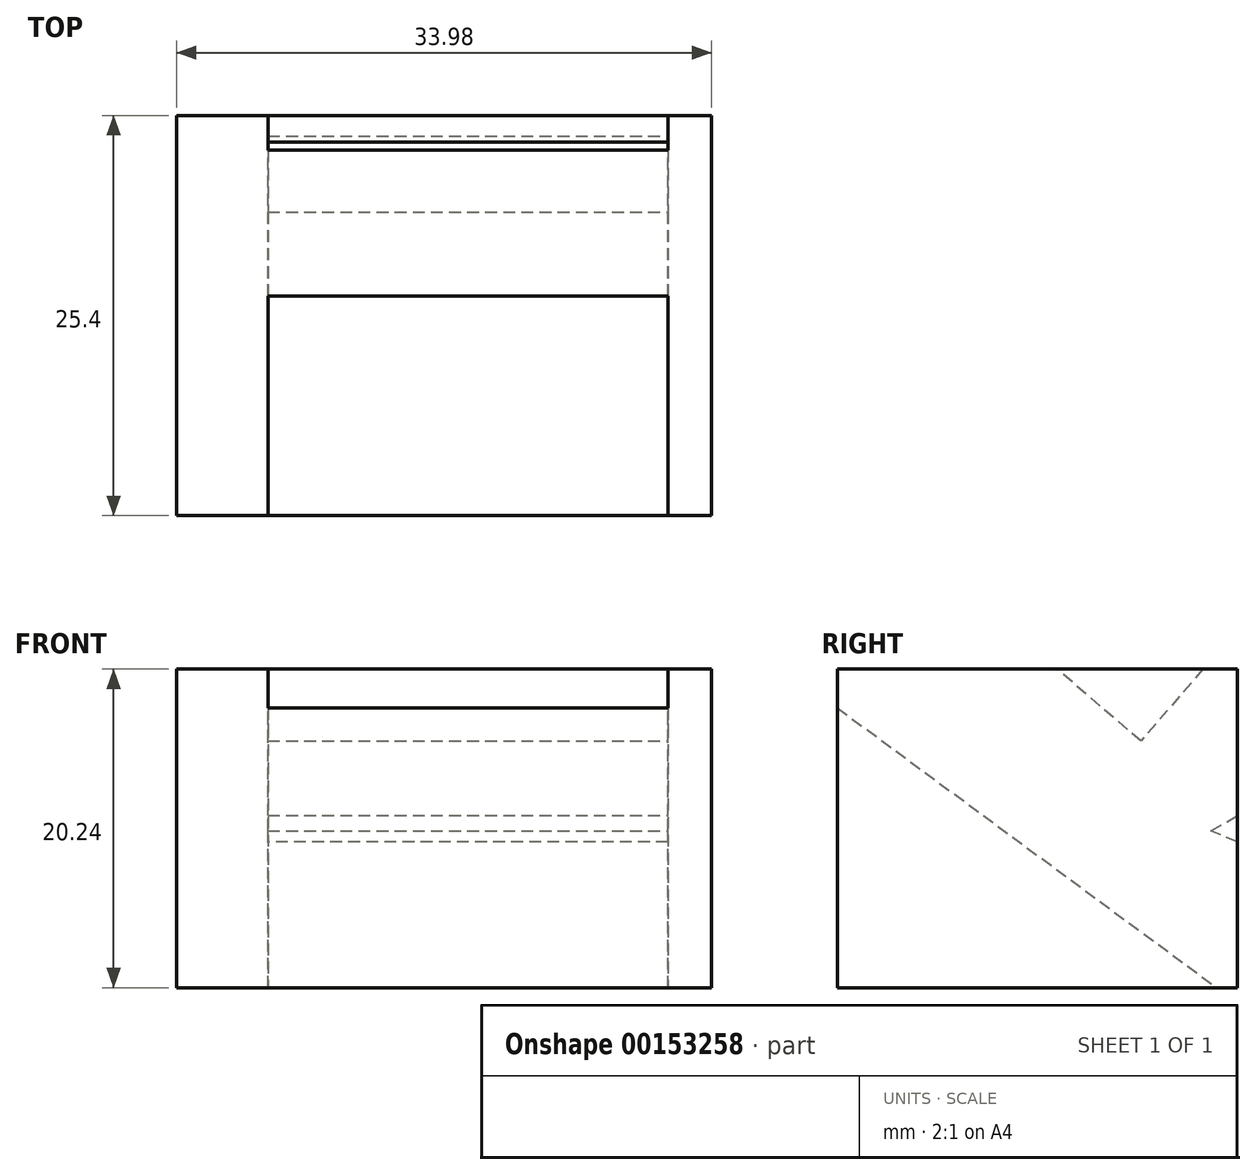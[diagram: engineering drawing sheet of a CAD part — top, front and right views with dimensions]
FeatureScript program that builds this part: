
annotation { "Feature Type Name" : "Feature", "Feature Type Description" : "" }
export const myFeature = defineFeature(function(context is Context, id is Id, definition is map)
    precondition{}
    {
        {
            var Q0;
            Q0=qCreatedBy(makeId("Front.planeOp"),FACE);
            var sketch = newSketch(context, id + "F0", { "sketchPlane" : qUnion([Q0])});
            skLineSegment(sketch, "E0.bottom", {"start": v(-18.5, 22.23) * mm, "end": v(15.48, 22.23) * mm});
            skLineSegment(sketch, "E0.top", {"start": v(-18.5, 1.99) * mm, "end": v(15.48, 1.99) * mm});
            skLineSegment(sketch, "E0.left", {"start": v(-18.5, 22.23) * mm, "end": v(-18.5, 1.99) * mm});
            skLineSegment(sketch, "E0.right", {"start": v(15.48, 22.23) * mm, "end": v(15.48, 1.99) * mm});
            skSolve(sketch);
        }
        {
            var Q0;
            Q0 = qSketchRegion(id + "F0", true);
            extrude(context, id + "F1", {"entities" : qUnion([Q0]), "depth" : 25.4 * mm});
        }
        {
            var Q0;
            Q0=qCreatedBy(makeId("Right.planeOp"),FACE);
            var sketch = newSketch(context, id + "F2", { "sketchPlane" : qUnion([Q0])});
            skLineSegment(sketch, "E1", {"start": v(-39.44, 30.1) * mm, "end": v(11.02, -7.1) * mm});
            skLineSegment(sketch, "E2", {"start": v(11.02, -7.1) * mm, "end": v(15.88, 4.72) * mm});
            skLineSegment(sketch, "E3", {"start": v(15.88, 4.72) * mm, "end": v(-1.68, 11.94) * mm});
            skLineSegment(sketch, "E4", {"start": v(-1.68, 11.94) * mm, "end": v(7.32, 17.2) * mm});
            skLineSegment(sketch, "E5", {"start": v(7.32, 17.2) * mm, "end": v(0, 26.2) * mm});
            skLineSegment(sketch, "E6", {"start": v(1.21, 26.2) * mm, "end": v(-6.14, 17.65) * mm});
            skLineSegment(sketch, "E7", {"start": v(-6.14, 17.65) * mm, "end": v(-31.79, 39.7) * mm});
            skLineSegment(sketch, "E8", {"start": v(-31.79, 39.7) * mm, "end": v(-39.44, 30.1) * mm});
            skSolve(sketch);
        }
        {
            var Q0;
            Q0=makeQuery(id+"F2.imprint","IMPRINT",FACE,{"disambiguationData":[TD([[makeQuery(id+"F2.imprint","IMPRINT",EDGE,{"derivedFrom":sQuery(id+"F2.wireOp",EDGE,"E1")}),1.0]])]});
            extrude(context, id + "F3", {"entities" : qUnion([Q0]), "operationType" : NewBodyOperationType.REMOVE, "endBound" : BoundingType.SYMMETRIC, "oppositeDirection" : true, "depth" : 25.4 * mm});
        }
    });
